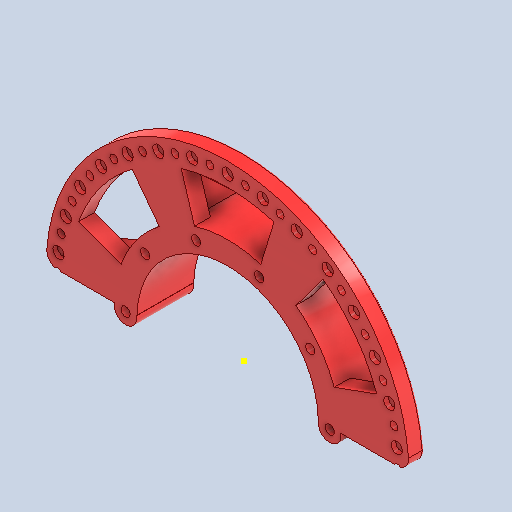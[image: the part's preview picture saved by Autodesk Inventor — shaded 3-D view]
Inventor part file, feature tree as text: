
AUTODESK INVENTOR PART (.ipt)
format: ipt  version: 2024 (Build 280153000, 153)  size: 385,024 bytes
history: native  units: mm
features: sketch x8, extrude x3, hole x3, pattern_circular x3, projected_geometry x3, fillet x2, other x1, revolve x1
ambient origin geometry x8: Origin, YZ Plane, XZ Plane, XY Plane, X Axis, Y Axis, Z Axis, Center Point
bodies: Body1 (feature_tree)
feature tree (24):
  other  "ソリッド1"
  extrude  "押し出し1"  Depth=160.0mm
  hole  "穴1"  [1 undecoded]
  pattern_circular  "円形状パターン1"  Count=8  [1 undecoded]
  extrude  "押し出し2"  Depth=100.0mm
  extrude  "押し出し3"  Depth=1.0mm
  revolve  "回転1"
  hole  "穴2"  [1 undecoded]
  pattern_circular  "円形状パターン2"  [2 undecoded]
  fillet  "フィレット1"  Radius=5.759587mm
  fillet  "フィレット2"  Radius=7.0mm
  hole  "穴3"  [1 undecoded]
  pattern_circular  "円形状パターン3"  [2 undecoded]
  sketch  "スケッチ8"
  sketch  "スケッチ1"
  sketch  "スケッチ2"
  sketch  "スケッチ3"
  projected_geometry  "投影ループ1"
  sketch  "スケッチ4"
  projected_geometry  "投影ループ2"
  sketch  "スケッチ5"
  projected_geometry  "投影ループ3"
  sketch  "スケッチ6"
  sketch  "スケッチ7"
note: 8 required parameter values undecoded (feature->parameter linkage not recoverable at this tier; creation-order binding heuristic only, values carry confidence <= 0.55)
